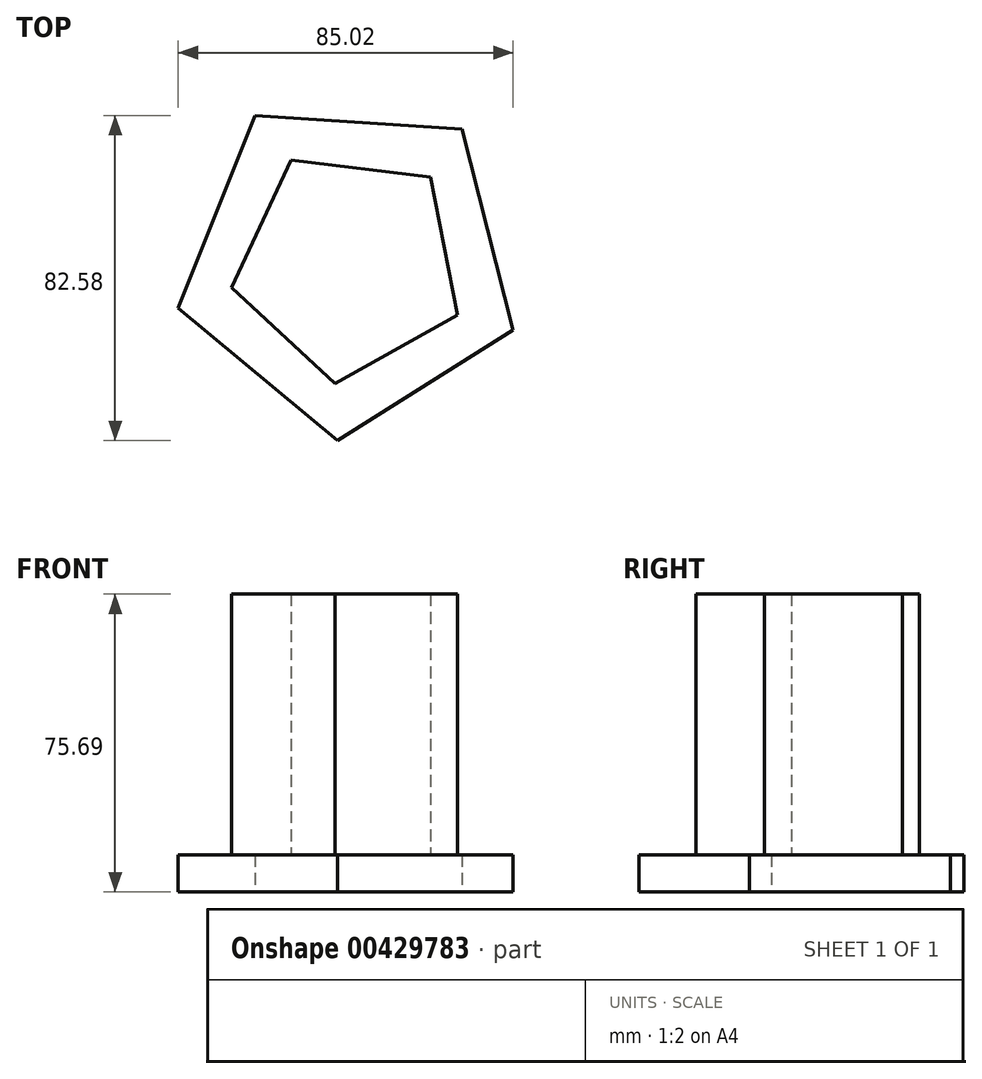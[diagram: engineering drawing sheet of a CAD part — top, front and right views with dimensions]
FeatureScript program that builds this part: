
annotation { "Feature Type Name" : "Feature", "Feature Type Description" : "" }
export const myFeature = defineFeature(function(context is Context, id is Id, definition is map)
    precondition{}
    {
        {
            var Q0;
            Q0=qCreatedBy(makeId("Top.planeOp"),FACE);
            var sketch = newSketch(context, id + "F0", { "sketchPlane" : qUnion([Q0])});
            skCircle(sketch, "E0.cCircle", {"center": v(0, 0) * mm, "radius": 36.24 * mm, "construction": true});
            skLineSegment(sketch, "E0.0", {"start": v(41.6, -16.6) * mm, "end": v(-2.92, -44.7) * mm});
            skLineSegment(sketch, "E0.1", {"start": v(-2.92, -44.7) * mm, "end": v(-43.41, -11.03) * mm});
            skLineSegment(sketch, "E0.2", {"start": v(-43.41, -11.03) * mm, "end": v(-23.9, 37.88) * mm});
            skLineSegment(sketch, "E0.3", {"start": v(-23.9, 37.88) * mm, "end": v(28.64, 34.44) * mm});
            skLineSegment(sketch, "E0.4", {"start": v(28.64, 34.44) * mm, "end": v(41.6, -16.6) * mm});
            skPoint(sketch, "E0.0.midPoint", {"position": v(19.34, -30.65) * mm});
            skSolve(sketch);
        }
        {
            var Q0;
            Q0=makeQuery(id+"F0.imprint","IMPRINT",FACE,{"disambiguationData":[TD([[makeQuery(id+"F0.imprint","IMPRINT",EDGE,{"derivedFrom":sQuery(id+"F0.wireOp",EDGE,"E0.0")}),-1.0]])]});
            extrude(context, id + "F1", {"entities" : qUnion([Q0]), "depth" : 9.4 * mm});
        }
        {
            var Q0;
            Q0=qCreatedBy(makeId("Top.planeOp"),FACE);
            var sketch = newSketch(context, id + "F2", { "sketchPlane" : qUnion([Q0])});
            skCircle(sketch, "E1.cCircle", {"center": v(0, 0) * mm, "radius": 24.58 * mm, "construction": true});
            skLineSegment(sketch, "E1.0", {"start": v(27.57, -12.77) * mm, "end": v(-3.62, -30.17) * mm});
            skLineSegment(sketch, "E1.1", {"start": v(-3.62, -30.17) * mm, "end": v(-29.81, -5.88) * mm});
            skLineSegment(sketch, "E1.2", {"start": v(-29.81, -5.88) * mm, "end": v(-14.8, 26.53) * mm});
            skLineSegment(sketch, "E1.3", {"start": v(-14.8, 26.53) * mm, "end": v(20.66, 22.28) * mm});
            skLineSegment(sketch, "E1.4", {"start": v(20.66, 22.28) * mm, "end": v(27.57, -12.77) * mm});
            skPoint(sketch, "E1.0.midPoint", {"position": v(11.98, -21.47) * mm});
            skSolve(sketch);
        }
        {
            var Q0;
            Q0=makeQuery(id+"F2.imprint","IMPRINT",FACE,{"disambiguationData":[TD([[makeQuery(id+"F2.imprint","IMPRINT",EDGE,{"derivedFrom":sQuery(id+"F2.wireOp",EDGE,"E1.0")}),-1.0]])]});
            extrude(context, id + "F3", {"entities" : qUnion([Q0]), "operationType" : NewBodyOperationType.ADD, "depth" : 50.3 * mm});
        }
        {
            var Q0;
            Q0=makeQuery(id+"F3.opExtrude","CAP_FACE",FACE,{"disambiguationData":[OSD([sQuery(id+"F2.wireOp",EDGE,"E1.0"),sQuery(id+"F2.wireOp",EDGE,"E1.1"),sQuery(id+"F2.wireOp",EDGE,"E1.2"),sQuery(id+"F2.wireOp",EDGE,"E1.3"),sQuery(id+"F2.wireOp",EDGE,"E1.4")])],"isStart":false});
            extrude(context, id + "F4", {"entities" : qUnion([Q0]), "operationType" : NewBodyOperationType.ADD, "depth" : 25.4 * mm});
        }
        {
            var Q0;
            {var subQ0=sQuery(id+"F2.wireOp",EDGE,"E1.4");Q0=makeQuery(id+"F4.boolean.opBoolean","MERGE",FACE,{"derivedFrom":[makeQuery(id+"F3.opExtrude","SWEPT_FACE",FACE,{"disambiguationData":[OSD([subQ0])]}),makeQuery(id+"F4.opExtrude","SWEPT_FACE",FACE,{"disambiguationData":[OSD([subQ0])]})]});}
            var sketch = newSketch(context, id + "F5", { "sketchPlane" : qUnion([Q0])});
            skPoint(sketch, "E2.firstSnap0", {"position": v(-17.86, 42.55) * mm});
            skLineSegment(sketch, "E2.bottom", {"start": v(-6.76, 42.55) * mm, "end": v(7.72, 42.55) * mm});
            skLineSegment(sketch, "E2.top", {"start": v(-6.76, 18.64) * mm, "end": v(7.72, 18.64) * mm});
            skLineSegment(sketch, "E2.left", {"start": v(-6.76, 42.55) * mm, "end": v(-6.76, 18.64) * mm});
            skLineSegment(sketch, "E2.right", {"start": v(7.72, 42.55) * mm, "end": v(7.72, 18.64) * mm});
            skSolve(sketch);
        }
        {
            var Q0;
            Q0=makeQuery(id+"F5.imprint","IMPRINT",FACE,{"disambiguationData":[TD([[makeQuery(id+"F5.imprint","IMPRINT",EDGE,{"derivedFrom":sQuery(id+"F5.wireOp",EDGE,"E2.bottom")}),-1.0]])]});
            var sketch = newSketch(context, id + "F6", { "sketchPlane" : qUnion([Q0])});
            skSolve(sketch);
        }
        {
            var Q0;
            Q0=makeQuery(id+"F6.imprint","IMPRINT",FACE,{"disambiguationData":[TD([[makeQuery(id+"F6.imprint","IMPRINT",EDGE,{"derivedFrom":makeQuery(id+"F5.imprint","IMPRINT",EDGE,{"derivedFrom":sQuery(id+"F5.wireOp",EDGE,"E2.bottom")})}),-1.0]])]});
            extrude(context, id + "F7", {"entities" : qUnion([Q0]), "operationType" : NewBodyOperationType.ADD, "oppositeDirection" : true, "depth" : 8.9 * mm});
        }
    });
